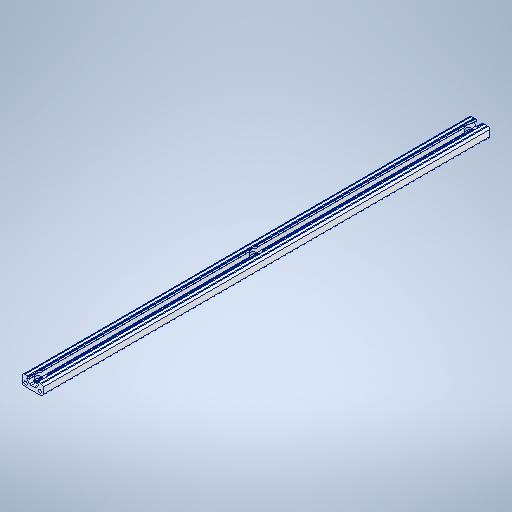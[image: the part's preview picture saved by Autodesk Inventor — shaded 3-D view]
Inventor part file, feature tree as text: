
AUTODESK INVENTOR PART (.ipt)
format: ipt  version: 2025 (Build 290162000, 162)  size: 384,000 bytes
history: native  units: mm
features: sketch x2, hole x2, extrude x1, mirror x1
ambient origin geometry x8: Origin, YZ Plane, XZ Plane, XY Plane, X Axis, Y Axis, Z Axis, Center Point
bodies: Solid1 (feature_tree)
feature tree (6):
  sketch  "Sketch1"  dims[d0=263.0mm d1=263.0mm]
  hole  "Hole1"  [1 undecoded]
  hole  "Hole2"  [1 undecoded]
  extrude  "Extrusion1"  TaperAngle=0.0deg  [1 undecoded]
  sketch  "Sketch2"  dims[d2=10.0mm d3=5.105mm d4=5.984mm d5=5.055mm d6=2.0mm d7=14.3mm d8=10.688mm d9=20.594885mm d10=12.0mm d11=6.0mm d12=9.779mm d13=2.0mm d14=14.3mm d15=10.688mm d16=20.594885mm d17=10.0mm d18=0.0mm d19=0.0mm]
  mirror  "Mirror1"
note: 3 required parameter values undecoded (feature->parameter linkage not recoverable at this tier; creation-order binding heuristic only, values carry confidence <= 0.55)
